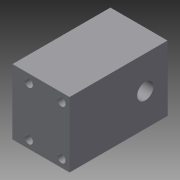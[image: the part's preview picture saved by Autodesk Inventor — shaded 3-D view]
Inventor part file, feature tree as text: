
AUTODESK INVENTOR PART (.ipt)
format: ipt  version: 2014 (Build 180170000, 170)  size: 100,352 bytes
history: native  units: in
note: dims shown in document units (in); Inventor stores cm internally (conversion verified against a paired STEP export)
features: sketch x3, extrude x2, hole x1
ambient origin geometry x8: Origin, YZ Plane, XZ Plane, XY Plane, X Axis, Y Axis, Z Axis, Center Point
bodies: Solid1 (feature_tree)
feature tree (6):
  extrude  "Extrusion1"  Depth=2.0in
  extrude  "Extrusion2"  Depth=1.75in
  hole  "Hole1"  [1 undecoded]
  sketch  "Sketch1"  dims[d0=3.0in d1=2.0in]
  sketch  "Sketch2"  dims[d2=1.75in d3=0.0in d4=0.5in]
  sketch  "Sketch3"  dims[d5=1.0in d6=2.32in d7=1.5in d8=0.0in d9=0.25in d10=0.25in d11=0.25in d12=0.5in d13=0.5in d14=0.25in d15=0.25in d16=0.25in d17=0.25in d18=0.75in d19=0.375in d20=0.25in d21=0.5635in d22=1.0in d23=0.8108in]
note: 1 required parameter value undecoded (feature->parameter linkage not recoverable at this tier; creation-order binding heuristic only, values carry confidence <= 0.55)
